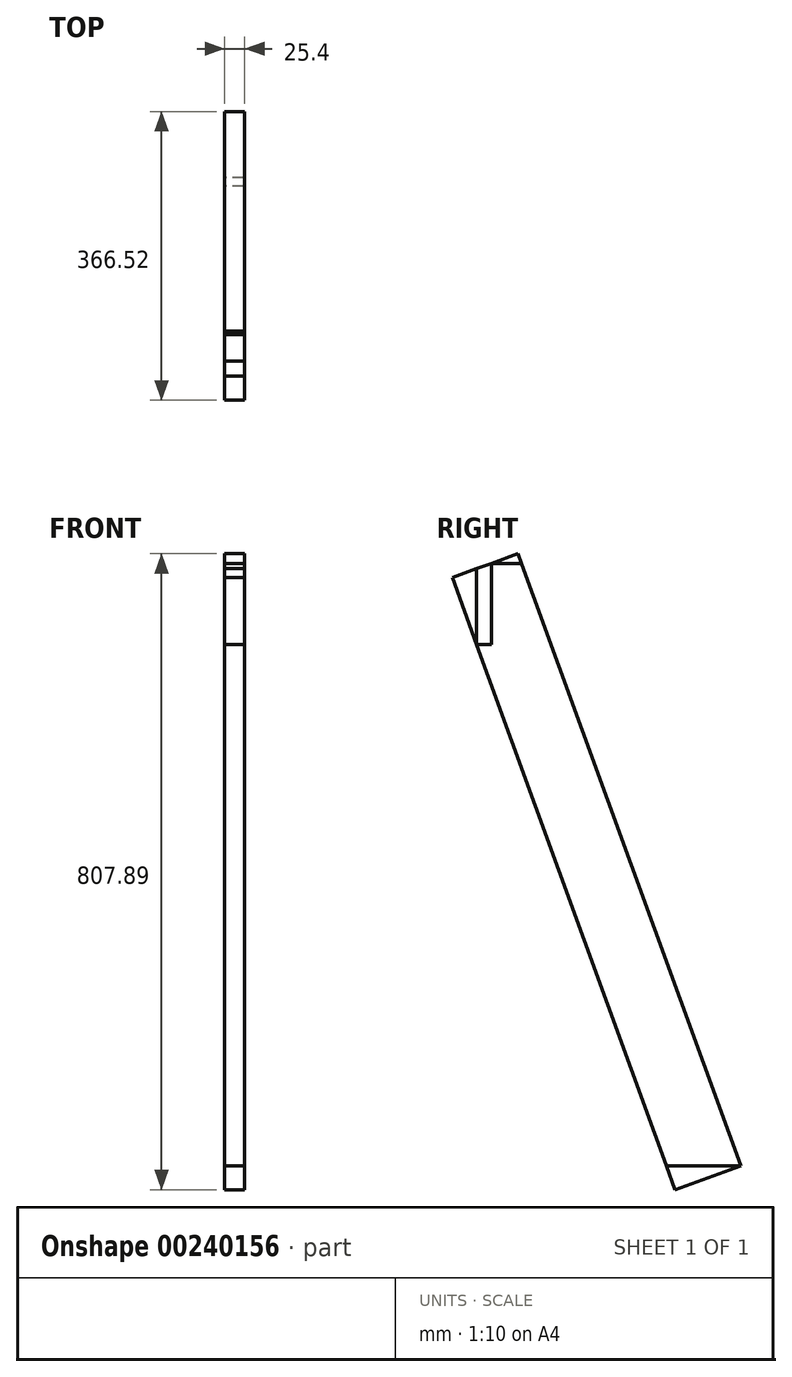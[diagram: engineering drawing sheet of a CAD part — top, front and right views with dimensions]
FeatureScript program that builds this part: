
annotation { "Feature Type Name" : "Feature", "Feature Type Description" : "" }
export const myFeature = defineFeature(function(context is Context, id is Id, definition is map)
    precondition{}
    {
        {
            var Q0;
            Q0=qCreatedBy(makeId("Right.planeOp"),FACE);
            var sketch = newSketch(context, id + "F0", { "sketchPlane" : qUnion([Q0])});
            skLineSegment(sketch, "E0", {"start": v(638.66, 215.22) * mm, "end": v(657.71, 215.22) * mm});
            skLineSegment(sketch, "E1", {"start": v(638.66, 215.22) * mm, "end": v(638.66, -446.86) * mm, "construction": true});
            skLineSegment(sketch, "E2", {"start": v(638.66, -446.86) * mm, "end": v(1692.85, -446.86) * mm, "construction": true});
            skLineSegment(sketch, "E3", {"start": v(657.71, 215.22) * mm, "end": v(657.71, 318.41) * mm});
            skLineSegment(sketch, "E4", {"start": v(638.66, 215.22) * mm, "end": v(879.64, -446.86) * mm});
            skLineSegment(sketch, "E5.0", {"start": v(691.27, 330.62) * mm, "end": v(974.25, -446.86) * mm});
            skLineSegment(sketch, "E6", {"start": v(657.71, 318.41) * mm, "end": v(695.71, 318.41) * mm});
            skLineSegment(sketch, "E7", {"start": v(638.66, 215.22) * mm, "end": v(607.73, 300.22) * mm});
            skLineSegment(sketch, "E8", {"start": v(691.27, 330.62) * mm, "end": v(607.73, 300.22) * mm});
            skLineSegment(sketch, "E9", {"start": v(879.64, -446.86) * mm, "end": v(974.25, -446.86) * mm});
            skLineSegment(sketch, "E10", {"start": v(974.25, -446.86) * mm, "end": v(890.71, -477.27) * mm});
            skLineSegment(sketch, "E11", {"start": v(879.64, -446.86) * mm, "end": v(890.71, -477.27) * mm});
            skLineSegment(sketch, "E12", {"start": v(638.66, 215.22) * mm, "end": v(638.66, 311.48) * mm});
            skSolve(sketch);
        }
        {
            var Q0;
            {var subQ3=sQuery(id+"F0.wireOp",EDGE,"E6");Q0=makeQuery(id+"F0.imprint","IMPRINT",FACE,{"disambiguationData":[TD([[makeQuery(id+"F0.imprint","IMPRINT",EDGE,{"derivedFrom":subQ3}),1.0]])]});}
            extrude(context, id + "F1", {"entities" : qUnion([Q0]), "depth" : 25.4 * mm});
        }
        {
            var Q0;
            {var subQ0=sQuery(id+"F0.wireOp",EDGE,"E7");Q0=makeQuery(id+"F0.imprint","IMPRINT",FACE,{"disambiguationData":[TD([[makeQuery(id+"F0.imprint","IMPRINT",EDGE,{"derivedFrom":subQ0}),-1.0]])]});}
            extrude(context, id + "F2", {"entities" : qUnion([Q0]), "depth" : 25.4 * mm});
        }
        {
            var Q0;
            Q0=makeQuery(id+"F0.imprint","IMPRINT",FACE,{"disambiguationData":[TD([[makeQuery(id+"F0.imprint","IMPRINT",EDGE,{"derivedFrom":sQuery(id+"F0.wireOp",EDGE,"E9")}),-1.0]])]});
            extrude(context, id + "F3", {"entities" : qUnion([Q0]), "depth" : 25.4 * mm});
        }
        {
            var Q0;
            Q0=makeQuery(id+"F0.imprint","IMPRINT",FACE,{"disambiguationData":[TD([[makeQuery(id+"F0.imprint","IMPRINT",EDGE,{"derivedFrom":sQuery(id+"F0.wireOp",EDGE,"E0")}),1.0]])]});
            extrude(context, id + "F4", {"entities" : qUnion([Q0]), "depth" : 25.4 * mm});
        }
        {
            var Q0;
            Q0=makeQuery(id+"F0.imprint","IMPRINT",FACE,{"disambiguationData":[TD([[makeQuery(id+"F0.imprint","IMPRINT",EDGE,{"derivedFrom":sQuery(id+"F0.wireOp",EDGE,"E0")}),-1.0]])]});
            extrude(context, id + "F5", {"entities" : qUnion([Q0]), "depth" : 25.4 * mm});
        }
    });
